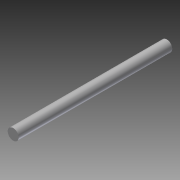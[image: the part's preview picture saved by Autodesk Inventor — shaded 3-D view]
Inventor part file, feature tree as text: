
AUTODESK INVENTOR PART (.ipt)
format: ipt  version: 2014 (Build 180170000, 170)  size: 69,120 bytes
history: native  units: in
note: dims shown in document units (in); Inventor stores cm internally (conversion verified against a paired STEP export)
features: extrude x1, sketch x1
ambient origin geometry x8: Origin, YZ Plane, XZ Plane, XY Plane, X Axis, Y Axis, Z Axis, Center Point
bodies: Solid1 (feature_tree)
feature tree (2):
  extrude  "Extrusion1"  Depth=7.0in TaperAngle=0.0deg
  sketch  "Sketch1"  dims[d0=0.5in d1=7.0in d2=0.0in]
